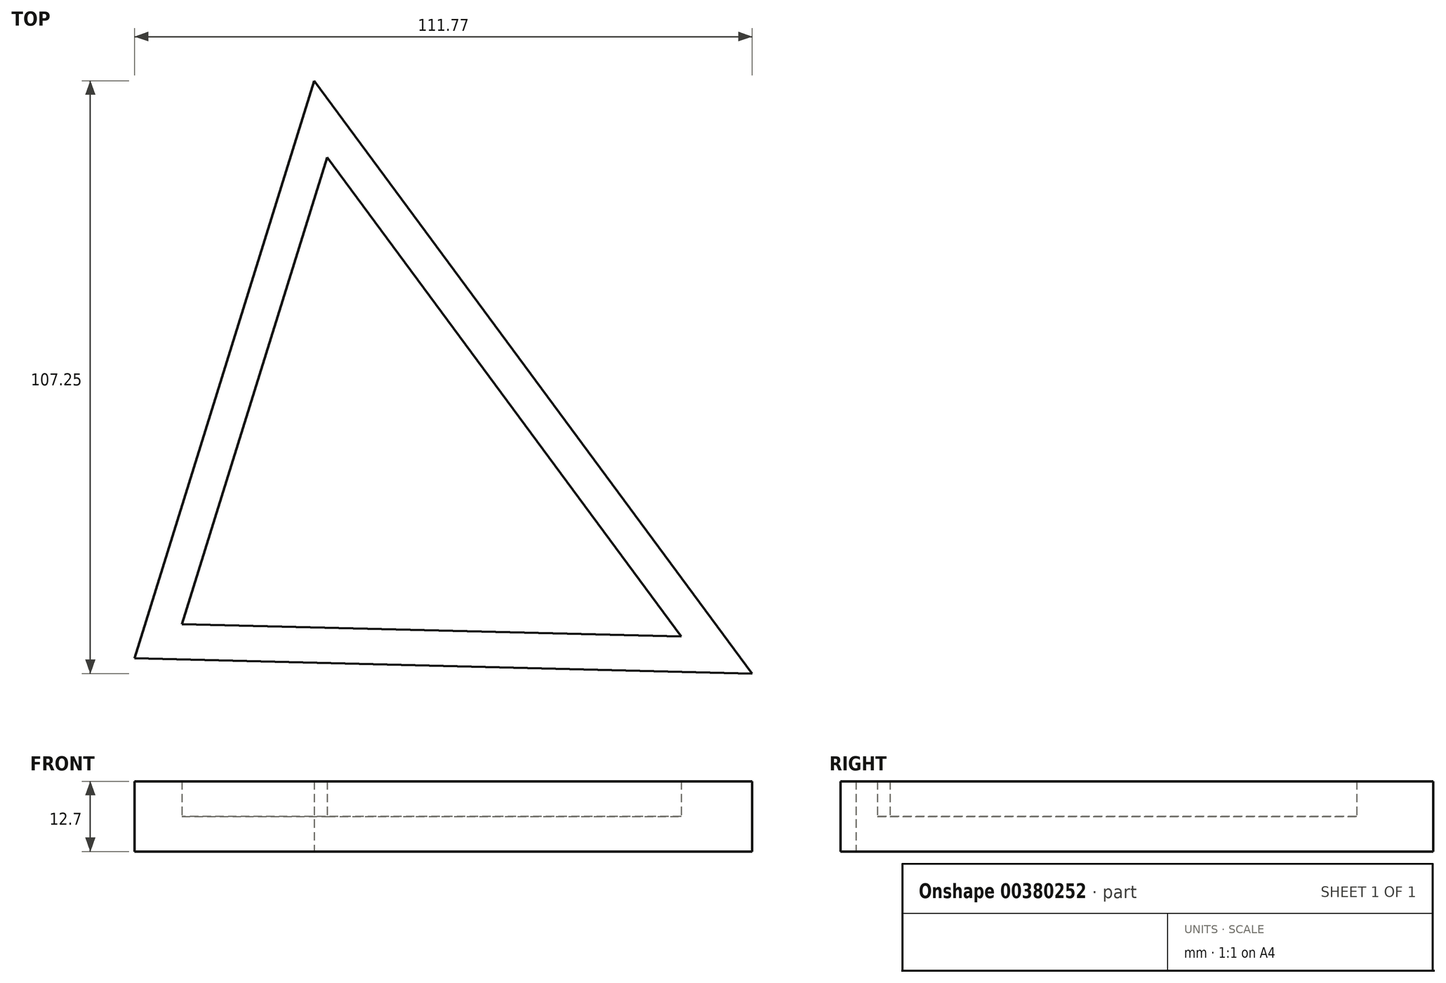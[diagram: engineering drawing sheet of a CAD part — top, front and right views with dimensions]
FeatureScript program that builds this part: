
annotation { "Feature Type Name" : "Feature", "Feature Type Description" : "" }
export const myFeature = defineFeature(function(context is Context, id is Id, definition is map)
    precondition{}
    {
        {
            var Q0;
            Q0=qCreatedBy(makeId("Top.planeOp"),FACE);
            var sketch = newSketch(context, id + "F0", { "sketchPlane" : qUnion([Q0])});
            skLineSegment(sketch, "E0", {"start": v(-74.04, -56.77) * mm, "end": v(-47.75, 27.7) * mm});
            skLineSegment(sketch, "E1", {"start": v(-47.75, 27.7) * mm, "end": v(16.34, -59.03) * mm});
            skLineSegment(sketch, "E2", {"start": v(16.34, -59.03) * mm, "end": v(-74.04, -56.77) * mm});
            skSolve(sketch);
        }
        {
            var Q0;
            Q0=makeQuery(id+"F0.imprint","IMPRINT",FACE,{"disambiguationData":[TD([[makeQuery(id+"F0.imprint","IMPRINT",EDGE,{"derivedFrom":sQuery(id+"F0.wireOp",EDGE,"E0")}),-1.0]])]});
            var Q1;
            Q1 = qSketchRegion(id + "F2", true);
            extrude(context, id + "F1", {"entities" : qUnion([Q0, Q1]), "depth" : 6.35 * mm});
        }
        {
            var Q0;
            Q0=makeQuery(id+"F1.opExtrude","CAP_FACE",FACE,{"disambiguationData":[OSD([sQuery(id+"F0.wireOp",EDGE,"E0"),sQuery(id+"F0.wireOp",EDGE,"E1"),sQuery(id+"F0.wireOp",EDGE,"E2")])],"isStart":false});
            var sketch = newSketch(context, id + "F2", { "sketchPlane" : qUnion([Q0])});
            skCircle(sketch, "E3", {"center": v(-39.05, -24.52) * mm, "radius": 19.17 * mm});
            skSolve(sketch);
        }
        {
            var Q0;
            Q0=makeQuery(id+"F1.opExtrude","CAP_FACE",FACE,{"disambiguationData":[OSD([sQuery(id+"F0.wireOp",EDGE,"E0"),sQuery(id+"F0.wireOp",EDGE,"E1"),sQuery(id+"F0.wireOp",EDGE,"E2")])],"isStart":false});
            shell(context, id + "F3", {"entities" : qUnion([Q0]), "thickness" : 6.35 * mm, "oppositeDirection" : true});
        }
    });
